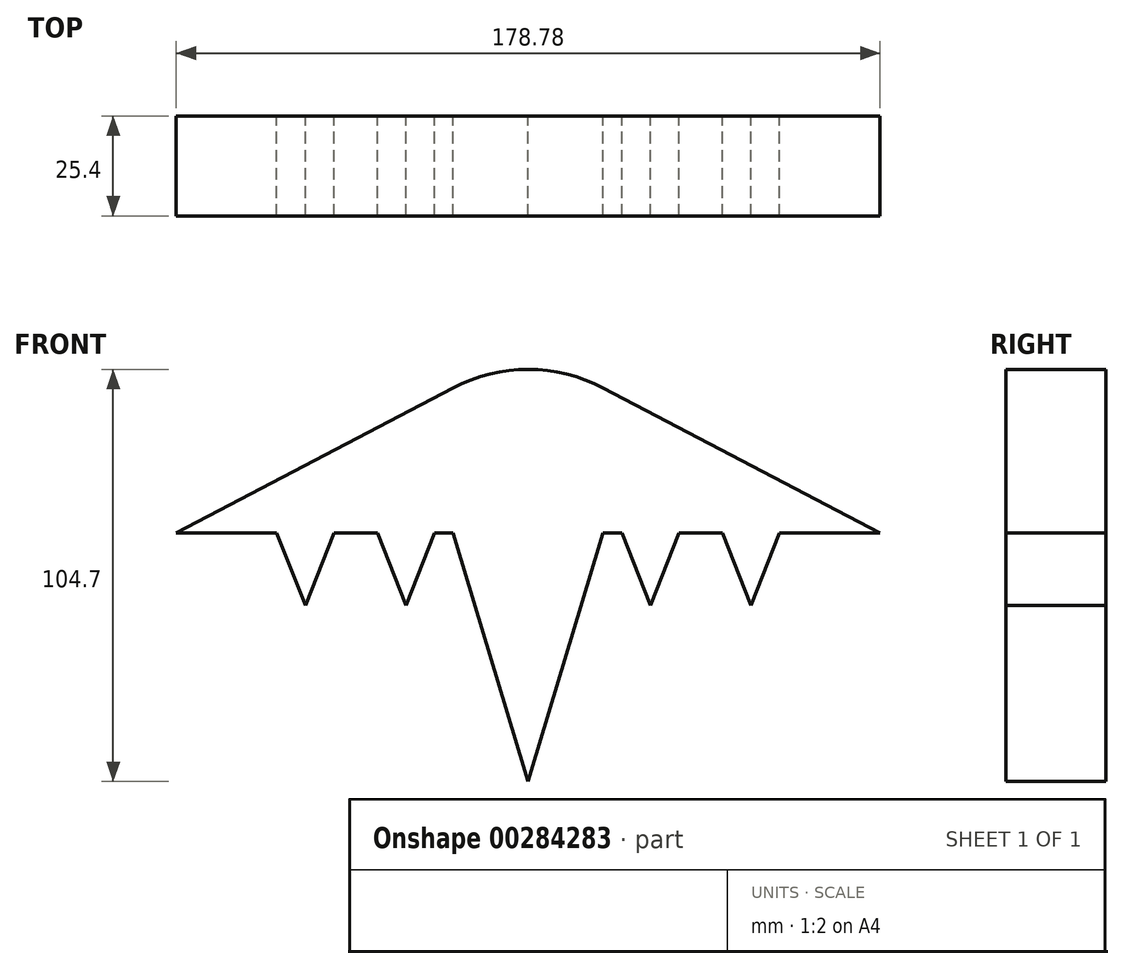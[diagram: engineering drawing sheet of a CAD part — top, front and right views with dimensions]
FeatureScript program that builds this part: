
annotation { "Feature Type Name" : "Feature", "Feature Type Description" : "" }
export const myFeature = defineFeature(function(context is Context, id is Id, definition is map)
    precondition{}
    {
        {
            var Q0;
            Q0=qCreatedBy(makeId("Front.planeOp"),FACE);
            var sketch = newSketch(context, id + "F0", { "sketchPlane" : qUnion([Q0])});
            skLineSegment(sketch, "E0", {"start": v(19.05, 18.5) * mm, "end": v(23.8, 18.5) * mm});
            skLineSegment(sketch, "E1", {"start": v(89.4, 18.5) * mm, "end": v(19.05, 55.33) * mm});
            skLineSegment(sketch, "E2", {"start": v(-19.05, 55.33) * mm, "end": v(-89.4, 18.5) * mm});
            skLineSegment(sketch, "E3", {"start": v(-89.4, 18.5) * mm, "end": v(-63.85, 18.5) * mm});
            skLineSegment(sketch, "E4", {"start": v(-19.05, 18.5) * mm, "end": v(0, -44.69) * mm});
            skLineSegment(sketch, "E5", {"start": v(0, -44.69) * mm, "end": v(19.05, 18.5) * mm});
            skPoint(sketch, "E6.orphan", {"position": v(-19.05, 4.51) * mm});
            skPoint(sketch, "E7.end.orphan", {"position": v(19.05, 4.51) * mm});
            skLineSegment(sketch, "E8", {"start": v(-38.31, 18.5) * mm, "end": v(-31.05, 0) * mm});
            skLineSegment(sketch, "E9", {"start": v(-31.05, 0) * mm, "end": v(-23.8, 18.5) * mm});
            skLineSegment(sketch, "E10", {"start": v(31.05, 0) * mm, "end": v(23.8, 18.5) * mm});
            skLineSegment(sketch, "E11", {"start": v(23.8, 18.5) * mm, "end": v(31.05, 0) * mm});
            skLineSegment(sketch, "E12", {"start": v(31.05, 0) * mm, "end": v(38.31, 18.5) * mm});
            skLineSegment(sketch, "E13.trimOffspring", {"start": v(38.31, 18.5) * mm, "end": v(49.33, 18.5) * mm});
            skLineSegment(sketch, "E14.trimOffspring", {"start": v(-23.8, 18.5) * mm, "end": v(-19.05, 18.5) * mm});
            skLineSegment(sketch, "E15", {"start": v(-49.33, 18.5) * mm, "end": v(-56.6, 0) * mm});
            skPoint(sketch, "E16.endSnap0", {"position": v(-63.85, 18.5) * mm});
            skPoint(sketch, "E16.end.orphan", {"position": v(-63.85, 16.34) * mm});
            skLineSegment(sketch, "E17", {"start": v(-56.6, 0) * mm, "end": v(-63.85, 18.5) * mm});
            skLineSegment(sketch, "E18.trimOffspring", {"start": v(-49.33, 18.5) * mm, "end": v(-38.31, 18.5) * mm});
            skLineSegment(sketch, "E19", {"start": v(49.33, 18.5) * mm, "end": v(56.6, 0) * mm});
            skLineSegment(sketch, "E20", {"start": v(56.6, 0) * mm, "end": v(63.85, 18.5) * mm});
            skLineSegment(sketch, "E21.trimOffspring", {"start": v(63.85, 18.5) * mm, "end": v(89.4, 18.5) * mm});
            skArc(sketch, "E22", {"start": v(-19.05, 55.33) * mm, "mid": v(0, 60.01) * mm, "end": v(19.05, 55.33) * mm});
            skSolve(sketch);
        }
        {
            var Q0;
            Q0 = qSketchRegion(id + "F0", true);
            extrude(context, id + "F1", {"entities" : qUnion([Q0]), "depth" : 25.4 * mm});
        }
    });
